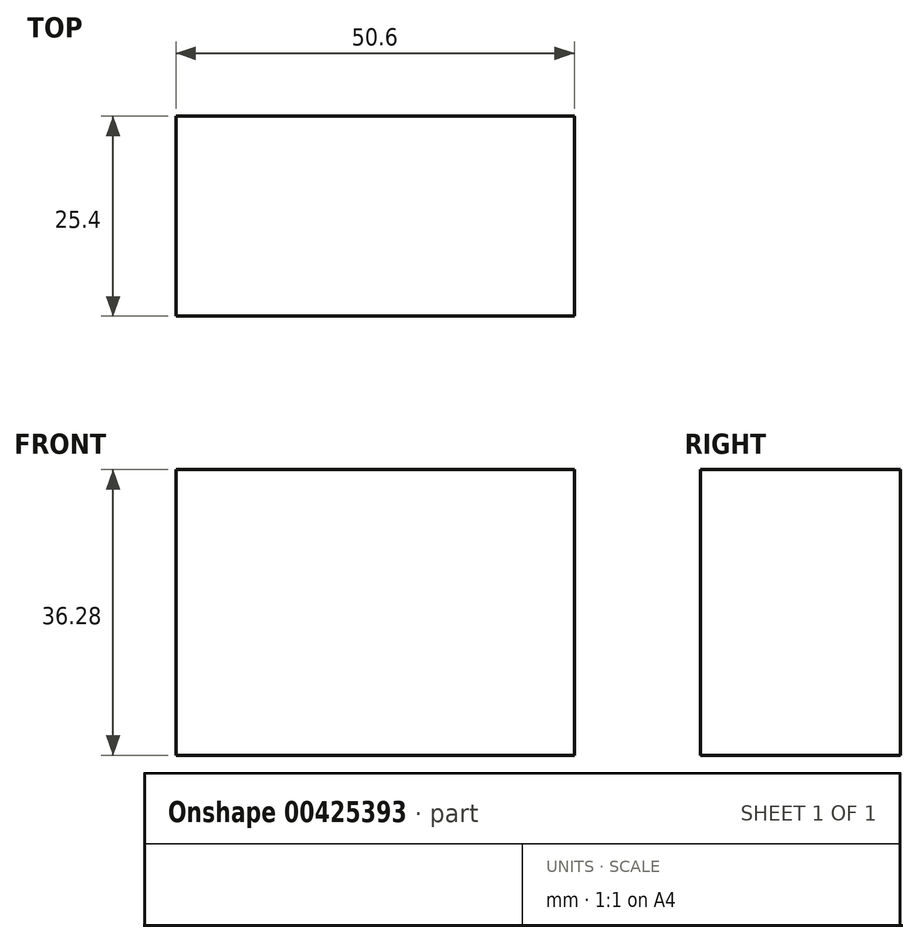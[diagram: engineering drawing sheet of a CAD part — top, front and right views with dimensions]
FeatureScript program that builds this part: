
annotation { "Feature Type Name" : "Feature", "Feature Type Description" : "" }
export const myFeature = defineFeature(function(context is Context, id is Id, definition is map)
    precondition{}
    {
        {
            var Q0;
            Q0=qCreatedBy(makeId("Front.planeOp"),FACE);
            var sketch = newSketch(context, id + "F0", { "sketchPlane" : qUnion([Q0])});
            skLineSegment(sketch, "E0.bottom", {"start": v(-50.6, 36.28) * mm, "end": v(0, 36.28) * mm});
            skLineSegment(sketch, "E0.top", {"start": v(-50.6, 0) * mm, "end": v(0, 0) * mm});
            skLineSegment(sketch, "E0.left", {"start": v(-50.6, 36.28) * mm, "end": v(-50.6, 0) * mm});
            skLineSegment(sketch, "E0.right", {"start": v(0, 36.28) * mm, "end": v(0, 0) * mm});
            skSolve(sketch);
        }
        {
            var Q0;
            Q0=makeQuery(id+"F0.imprint","IMPRINT",FACE,{"disambiguationData":[TD([[makeQuery(id+"F0.imprint","IMPRINT",EDGE,{"derivedFrom":sQuery(id+"F0.wireOp",EDGE,"E0.bottom")}),-1.0]])]});
            extrude(context, id + "F1", {"entities" : qUnion([Q0]), "depth" : 25.4 * mm});
        }
        {
            var Q0;
            Q0=qCreatedBy(makeId("Front.planeOp"),FACE);
            var sketch = newSketch(context, id + "F2", { "sketchPlane" : qUnion([Q0])});
            skLineSegment(sketch, "E1.bottom", {"start": v(-47.74, 17.95) * mm, "end": v(-21.58, 17.95) * mm});
            skLineSegment(sketch, "E1.top", {"start": v(-47.74, 0) * mm, "end": v(-21.58, 0) * mm});
            skLineSegment(sketch, "E1.left", {"start": v(-47.74, 17.95) * mm, "end": v(-47.74, 0) * mm});
            skLineSegment(sketch, "E1.right", {"start": v(-21.58, 17.95) * mm, "end": v(-21.58, 0) * mm});
            skSolve(sketch);
        }
        {
            var Q0;
            Q0=makeQuery(id+"F2.imprint","IMPRINT",FACE,{"disambiguationData":[TD([[makeQuery(id+"F2.imprint","IMPRINT",EDGE,{"derivedFrom":sQuery(id+"F2.wireOp",EDGE,"E1.bottom")}),-1.0]])]});
            var Q1;
            Q1=makeQuery(id+"F1.opExtrude","CAP_FACE",FACE,{"disambiguationData":[OSD([sQuery(id+"F0.wireOp",EDGE,"E0.bottom"),sQuery(id+"F0.wireOp",EDGE,"E0.top"),sQuery(id+"F0.wireOp",EDGE,"E0.left"),sQuery(id+"F0.wireOp",EDGE,"E0.right")])],"isStart":true});
            extrude(context, id + "F3", {"entities" : qUnion([Q0, Q1]), "operationType" : NewBodyOperationType.ADD, "depth" : 25.4 * mm});
        }
    });
